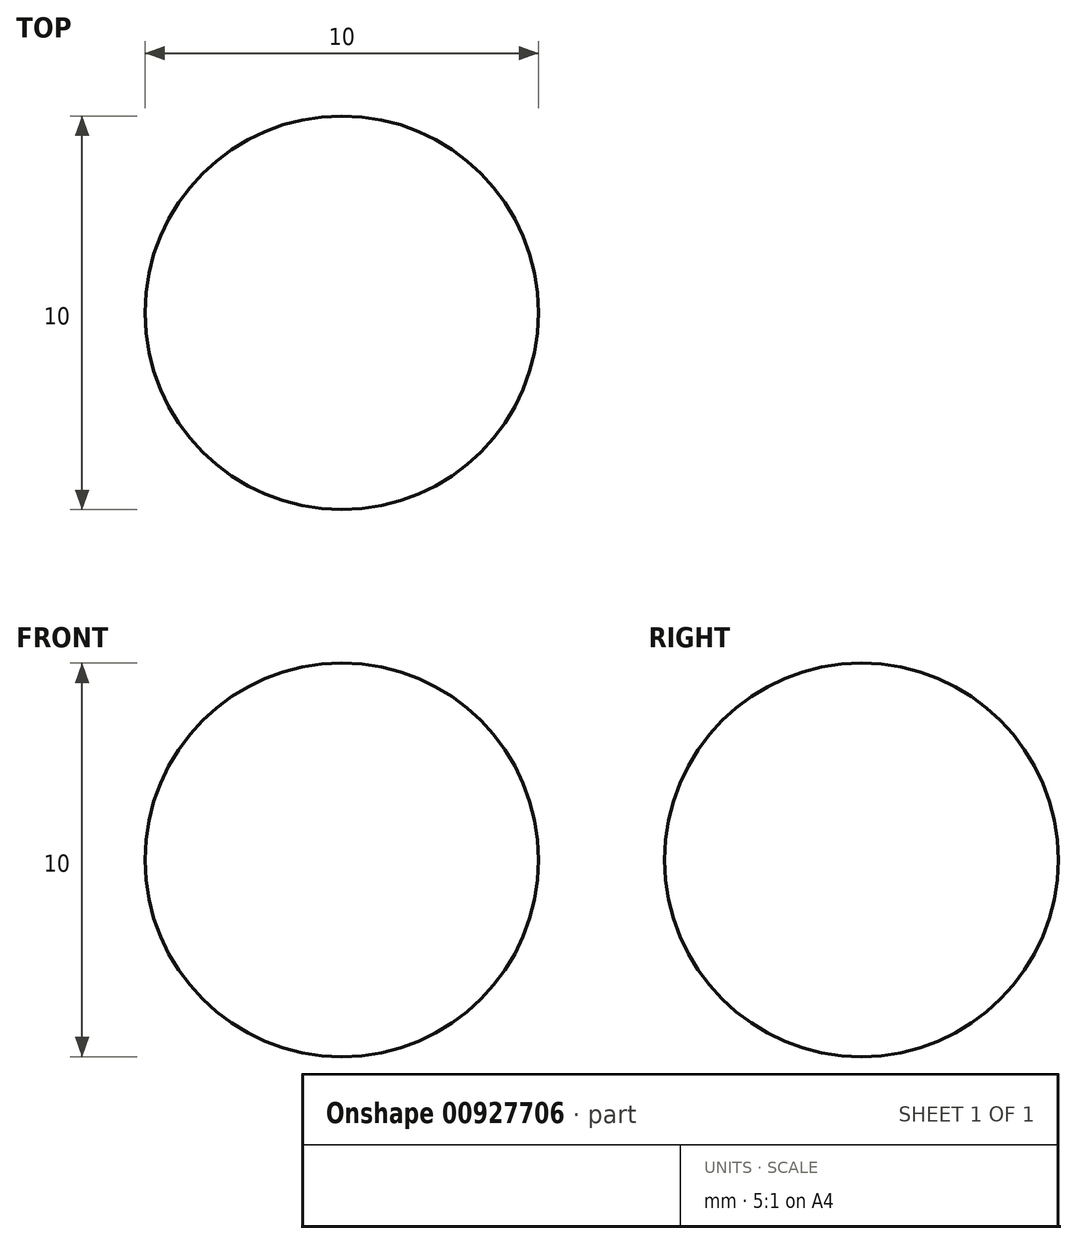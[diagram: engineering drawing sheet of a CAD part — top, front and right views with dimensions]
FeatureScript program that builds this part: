
annotation { "Feature Type Name" : "Feature", "Feature Type Description" : "" }
export const myFeature = defineFeature(function(context is Context, id is Id, definition is map)
    precondition{}
    {
        {
            var Q0;
            Q0=qCreatedBy(makeId("Front.planeOp"),FACE);
            var sketch = newSketch(context, id + "F0", { "sketchPlane" : qUnion([Q0])});
            skArc(sketch, "E0", {"start": v(0, 5) * mm, "mid": v(5, 0) * mm, "end": v(0, -5) * mm});
            skLineSegment(sketch, "E1", {"start": v(0, 5) * mm, "end": v(0, -5) * mm});
            skSolve(sketch);
        }
        {
            var Q0;
            Q0 = qSketchRegion(id + "F0", true);
            var Q1;
            Q1=sQuery(id+"F0.wireOp",EDGE,"E1");
            revolve(context, id + "F1", {"surfaceOperationType" : NewSurfaceOperationType.NEW, "entities" : qUnion([Q0]), "axis" : qUnion([Q1]), "revolveType" : RevolveType.FULL});
        }
    });
